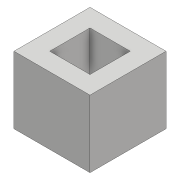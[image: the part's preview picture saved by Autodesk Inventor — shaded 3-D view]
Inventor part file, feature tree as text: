
AUTODESK INVENTOR PART (.ipt)
format: ipt  version: 2017 (Build 210142000, 142)  size: 84,992 bytes
history: native  units: mm
features: plane x1, extrude x1, sketch x1
ambient origin geometry x8: Origin, YZ Plane, XZ Plane, XY Plane, X Axis, Y Axis, Z Axis, Center Point
bodies: Solid2 (feature_tree)
feature tree (3):
  plane  "Work Plane1"
  extrude  "Extrusion2"  Depth=9.0mm
  sketch  "Sketch2"  dims[d4=9.0mm d5=9.0mm d6=10.0mm d7=5.0mm d8=0.0mm d9=0.0mm]
